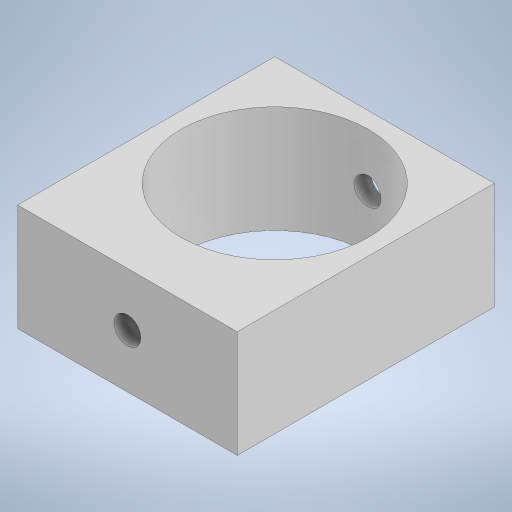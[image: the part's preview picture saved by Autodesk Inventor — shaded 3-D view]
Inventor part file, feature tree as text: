
AUTODESK INVENTOR PART (.ipt)
format: ipt  version: 2023 (Build 270158000, 158)  size: 286,208 bytes
history: native  units: in
note: dims shown in document units (in); Inventor stores cm internally (conversion verified against a paired STEP export)
features: extrude x5, sketch x5
ambient origin geometry x8: Origin, YZ Plane, XZ Plane, XY Plane, X Axis, Y Axis, Z Axis, Center Point
bodies: Solid1 (feature_tree)
feature tree (10):
  extrude  "Extrusion1"  Depth=1.6142in
  extrude  "Extrusion2"  Depth=0.8071in
  extrude  "Extrusion3"  Depth=0.7874in TaperAngle=0.0deg
  extrude  "Extrusion4"  Depth=0.1969in TaperAngle=0.0deg
  extrude  "Extrusion5"  Depth=0.1969in TaperAngle=0.0deg
  sketch  "Sketch1"  dims[d0=1.6142in d1=1.6142in]
  sketch  "Sketch3"  dims[d2=0.8071in d3=0.8071in]
  sketch  "Sketch4"  dims[d4=1.378in d5=0.7874in d6=0.0in]
  sketch  "Sketch5"  dims[d8=0.3543in d9=0.1969in d10=0.0in]
  sketch  "Sketch6"  dims[d11=0.1969in d12=0.1969in d13=0.0in d14=0.0787in d15=0.0in d16=0.1969in d17=0.0in]
